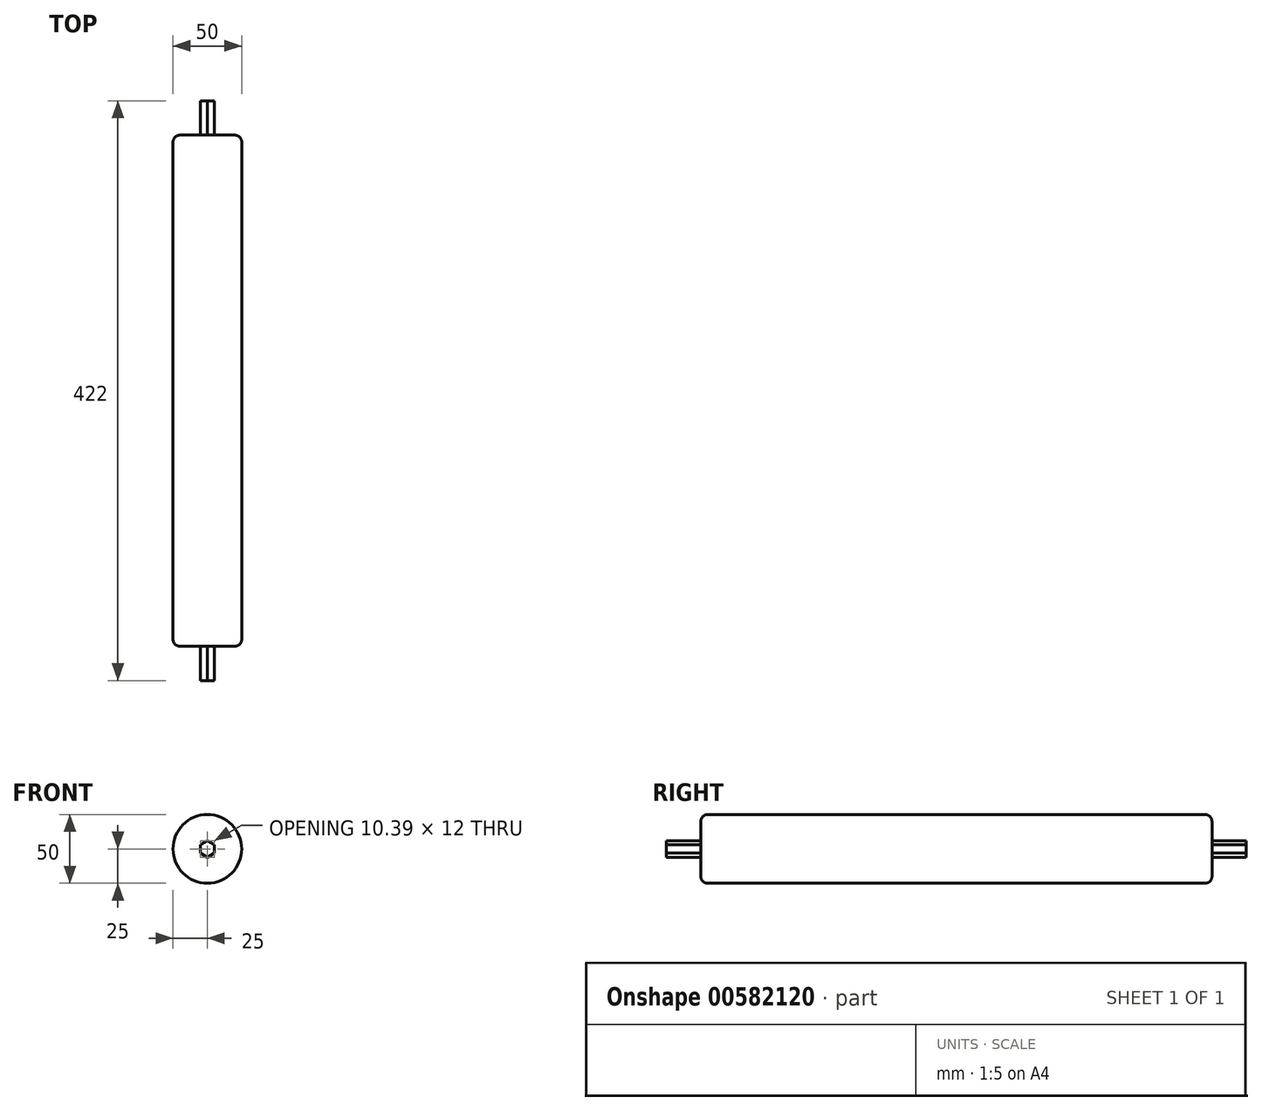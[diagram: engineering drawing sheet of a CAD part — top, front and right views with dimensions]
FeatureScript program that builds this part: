
annotation { "Feature Type Name" : "Feature", "Feature Type Description" : "" }
export const myFeature = defineFeature(function(context is Context, id is Id, definition is map)
    precondition{}
    {
        {
            var Q0;
            Q0=qCreatedBy(makeId("Front.planeOp"),FACE);
            var sketch = newSketch(context, id + "F0", { "sketchPlane" : qUnion([Q0])});
            skCircle(sketch, "E0", {"center": v(0, 0) * mm, "radius": 25 * mm});
            skSolve(sketch);
        }
        {
            var Q0;
            Q0=makeQuery(id+"F0.imprint","IMPRINT",FACE,{"disambiguationData":[TD([[makeQuery(id+"F0.imprint","IMPRINT",EDGE,{"derivedFrom":sQuery(id+"F0.wireOp",EDGE,"E0")}),1.0]])]});
            extrude(context, id + "F1", {"entities" : qUnion([Q0]), "depth" : 372 * mm, "offsetDistance" : 25 * mm});
        }
        {
            var Q0;
            Q0=makeQuery(id+"F1.opExtrude","CAP_EDGE",EDGE,{"disambiguationData":[OSD([sQuery(id+"F0.wireOp",EDGE,"E0")])],"isStart":false});
            var Q1;
            Q1=makeQuery(id+"F1.opExtrude","CAP_EDGE",EDGE,{"disambiguationData":[OSD([sQuery(id+"F0.wireOp",EDGE,"E0")])],"isStart":true});
            fillet(context, id + "F2", {"entities" : qUnion([Q0, Q1]), "radius" : 5 * mm, "tangentPropagation" : true, "allowEdgeOverflow" : false});
        }
        {
            var Q0;
            Q0=makeQuery(id+"F1.opExtrude","CAP_FACE",FACE,{"disambiguationData":[OSD([sQuery(id+"F0.wireOp",EDGE,"E0")])],"isStart":true});
            var sketch = newSketch(context, id + "F3", { "sketchPlane" : qUnion([Q0])});
            skCircle(sketch, "E1.cCircle", {"center": v(0, 0) * mm, "radius": 5.2 * mm, "construction": true});
            skLineSegment(sketch, "E1.0", {"start": v(5.2, -3) * mm, "end": v(0, -6) * mm});
            skLineSegment(sketch, "E1.1", {"start": v(0, -6) * mm, "end": v(-5.2, -3) * mm});
            skLineSegment(sketch, "E1.2", {"start": v(-5.2, -3) * mm, "end": v(-5.2, 3) * mm});
            skLineSegment(sketch, "E1.3", {"start": v(-5.2, 3) * mm, "end": v(0, 6) * mm});
            skLineSegment(sketch, "E1.4", {"start": v(0, 6) * mm, "end": v(5.2, 3) * mm});
            skLineSegment(sketch, "E1.5", {"start": v(5.2, 3) * mm, "end": v(5.2, -3) * mm});
            skPoint(sketch, "E1.0.midPoint", {"position": v(2.6, -4.5) * mm});
            skSolve(sketch);
        }
        {
            var Q0;
            Q0=qSketchRegion(id+"F3",true);
            extrude(context, id + "F4", {"entities" : qUnion([Q0]), "operationType" : NewBodyOperationType.ADD, "depth" : 25 * mm, "offsetDistance" : 25 * mm, "hasSecondDirection" : true, "secondDirectionOppositeDirection" : true, "secondDirectionDepth" : 397 * mm});
        }
    });
